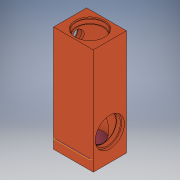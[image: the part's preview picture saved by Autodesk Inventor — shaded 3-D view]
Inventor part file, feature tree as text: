
AUTODESK INVENTOR PART (.ipt)
format: ipt  version: 2018 (Build 220112000, 112)  size: 179,200 bytes
history: native  units: in
note: dims shown in document units (in); Inventor stores cm internally (conversion verified against a paired STEP export)
features: sketch x10, extrude x9, plane x1, hole x1
ambient origin geometry x8: Origin, YZ Plane, XZ Plane, XY Plane, X Axis, Y Axis, Z Axis, Center Point
bodies: Solid1 (feature_tree)
feature tree (21):
  extrude  "Extrusion1"  Depth=1.25in
  plane  "Work Plane1"
  hole  "Hole1"  [1 undecoded]
  extrude  "Extrusion2"  Depth=1.1in
  extrude  "Extrusion4"  Depth=0.5in
  extrude  "Extrusion5"  Depth=4.0in TaperAngle=0.0deg
  extrude  "Extrusion3"  Depth=0.25in TaperAngle=0.0deg
  extrude  "Extrusion7"  Depth=4.0in TaperAngle=0.0deg
  extrude  "Extrusion8"  Depth=0.05in TaperAngle=0.0deg
  extrude  "Extrusion9"  Depth=0.2in TaperAngle=0.0deg
  extrude  "Extrusion10"  Depth=0.05in
  sketch  "Sketch1"  dims[d0=1.5in d1=1.25in]
  sketch  "Sketch2"  dims[d2=4.0in d3=0.0in]
  sketch  "Sketch3"  dims[d4=1.0in d5=0.75in d6=0.375in d7=0.25in d8=0.5635in d9=4.0in d10=0.8108in d11=-0.4in]
  sketch  "Sketch4"  dims[d12=1.0in d13=1.1in]
  sketch  "Sketch5"  dims[d14=0.1in d15=0.0in d16=0.5in]
  sketch  "Sketch6"  dims[d17=0.45in d18=4.0in d19=0.0in]
  sketch  "Sketch7"  dims[d20=1.0in d21=0.25in d22=0.0in]
  sketch  "Sketch8"  dims[d23=0.97in d24=4.0in d25=0.0in]
  sketch  "Sketch9"  dims[d26=0.55in d29=0.05in d30=0.0in]
  sketch  "Sketch10"  dims[d31=0.5in d32=0.2in d33=0.0in d34=1.05in d35=0.2in d36=0.0in d37=1.1in d38=0.05in d39=0.0in]
note: 1 required parameter value undecoded (feature->parameter linkage not recoverable at this tier; creation-order binding heuristic only, values carry confidence <= 0.55)
